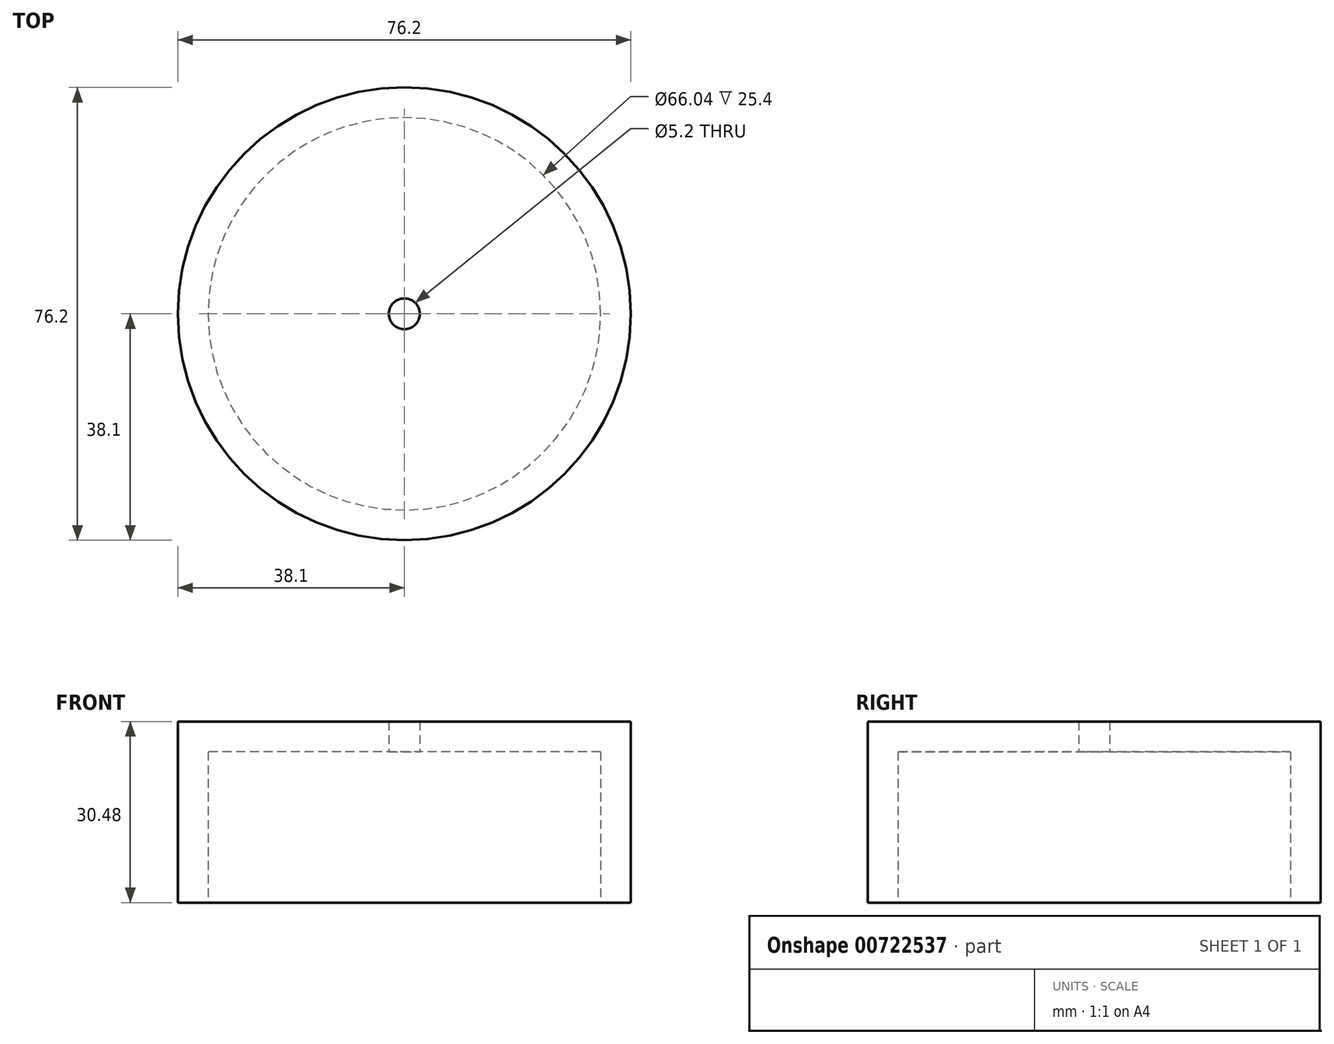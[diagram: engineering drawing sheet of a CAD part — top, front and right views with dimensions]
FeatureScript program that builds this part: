
annotation { "Feature Type Name" : "Feature", "Feature Type Description" : "" }
export const myFeature = defineFeature(function(context is Context, id is Id, definition is map)
    precondition{}
    {
        {
            var Q0;
            Q0=qCreatedBy(makeId("Top.planeOp"),FACE);
            var sketch = newSketch(context, id + "F0", { "sketchPlane" : qUnion([Q0])});
            skCircle(sketch, "E0", {"center": v(0, 0) * mm, "radius": 38.1 * mm});
            skCircle(sketch, "E1", {"center": v(0, 0) * mm, "radius": 33.02 * mm});
            skSolve(sketch);
        }
        {
            var Q0;
            Q0=makeQuery(id+"F0.imprint","IMPRINT",FACE,{"disambiguationData":[TD([[makeQuery(id+"F0.imprint","IMPRINT",EDGE,{"derivedFrom":sQuery(id+"F0.wireOp",EDGE,"E0")}),1.0]])]});
            extrude(context, id + "F1", {"entities" : qUnion([Q0]), "depth" : 25.4 * mm, "offsetDistance" : 25.4 * mm});
        }
        {
            var Q0;
            Q0=makeQuery(id+"F1.opExtrude","CAP_FACE",FACE,{"disambiguationData":[OSD([sQuery(id+"F0.wireOp",EDGE,"E0"),sQuery(id+"F0.wireOp",EDGE,"E1")])],"isStart":false});
            var sketch = newSketch(context, id + "F2", { "sketchPlane" : qUnion([Q0])});
            skCircle(sketch, "E2", {"center": v(0, 0) * mm, "radius": 38.1 * mm});
            skSolve(sketch);
        }
        {
            var Q0;
            Q0=qSketchRegion(id+"F2",true);
            extrude(context, id + "F3", {"entities" : qUnion([Q0]), "operationType" : NewBodyOperationType.ADD, "depth" : 5.08 * mm, "offsetDistance" : 25.4 * mm});
        }
        {
            var Q0;
            Q0=makeQuery(id+"F3.opExtrude","CAP_FACE",FACE,{"disambiguationData":[OSD([sQuery(id+"F2.wireOp",EDGE,"E2")])],"isStart":true});
            var sketch = newSketch(context, id + "F4", { "sketchPlane" : qUnion([Q0])});
            skCircle(sketch, "E3", {"center": v(0, 0) * mm, "radius": 2.6 * mm});
            skSolve(sketch);
        }
        {
            var Q0;
            Q0=makeQuery(id+"F4.imprint","IMPRINT",FACE,{"disambiguationData":[TD([[makeQuery(id+"F4.imprint","IMPRINT",EDGE,{"derivedFrom":sQuery(id+"F4.wireOp",EDGE,"E3")}),1.0]])]});
            extrude(context, id + "F5", {"entities" : qUnion([Q0]), "operationType" : NewBodyOperationType.REMOVE, "oppositeDirection" : true, "depth" : 228.6 * mm, "offsetDistance" : 25.4 * mm});
        }
    });
